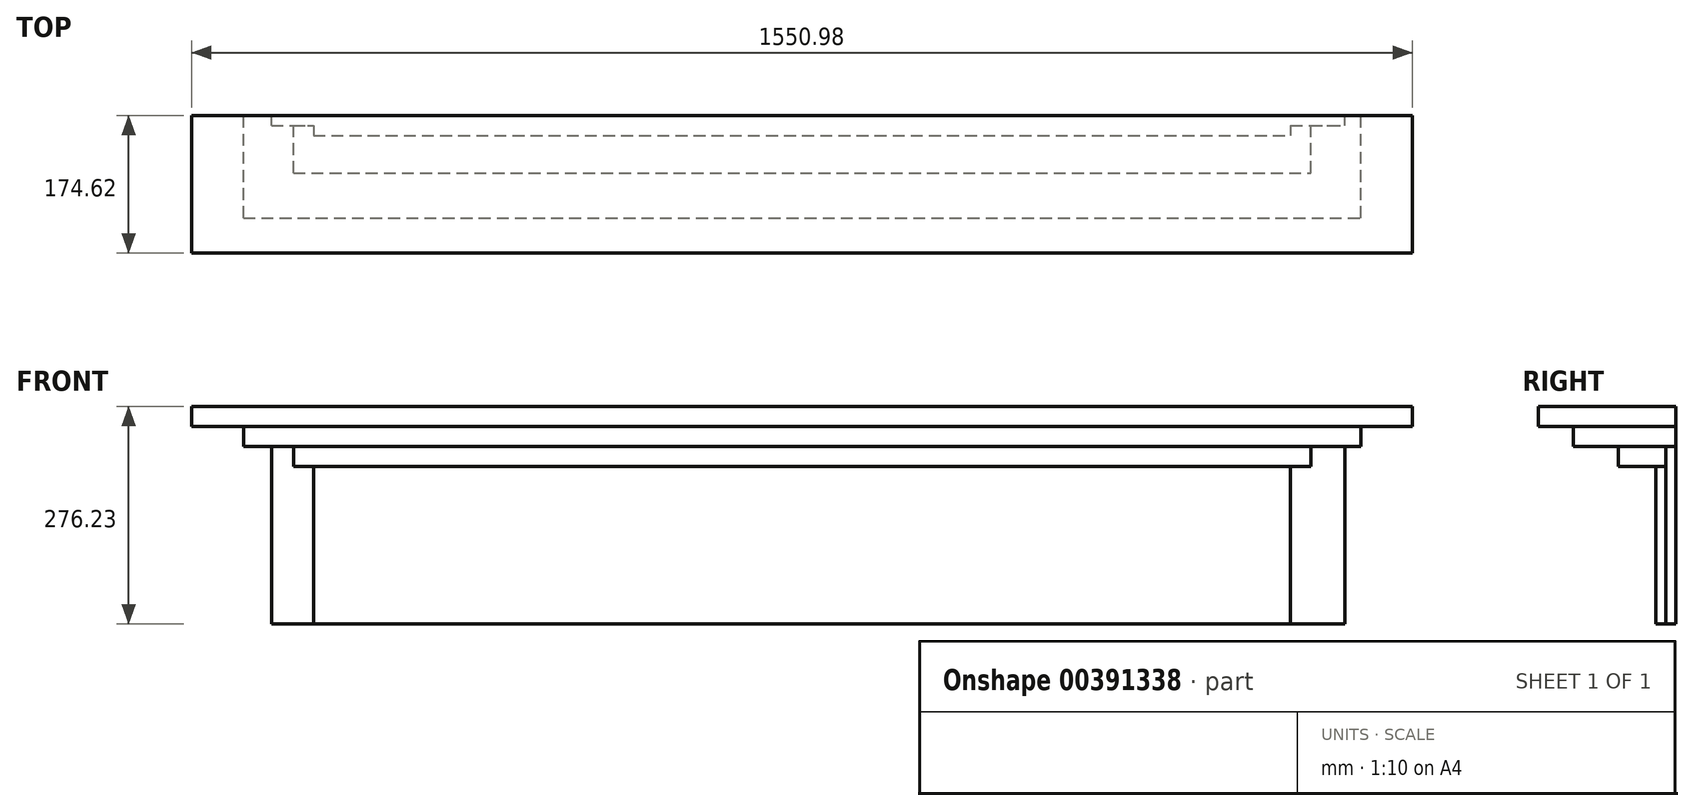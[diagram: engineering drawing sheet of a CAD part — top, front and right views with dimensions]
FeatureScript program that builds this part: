
annotation { "Feature Type Name" : "Feature", "Feature Type Description" : "" }
export const myFeature = defineFeature(function(context is Context, id is Id, definition is map)
    precondition{}
    {
        {
            var Q0;
            Q0=qCreatedBy(makeId("Front.planeOp"),FACE);
            var sketch = newSketch(context, id + "F0", { "sketchPlane" : qUnion([Q0])});
            skLineSegment(sketch, "E0.bottom", {"start": v(-775.5, 0) * mm, "end": v(775.5, 0) * mm});
            skLineSegment(sketch, "E0.top", {"start": v(-775.5, -25.4) * mm, "end": v(775.5, -25.4) * mm});
            skLineSegment(sketch, "E0.left", {"start": v(-775.5, 0) * mm, "end": v(-775.5, -25.4) * mm});
            skLineSegment(sketch, "E0.right", {"start": v(775.5, 0) * mm, "end": v(775.5, -25.4) * mm});
            skSolve(sketch);
        }
        {
            var Q0;
            Q0 = qSketchRegion(id + "F0", true);
            extrude(context, id + "F1", {"entities" : qUnion([Q0]), "depth" : 174.62 * mm});
        }
        {
            var Q0;
            Q0=qCreatedBy(makeId("Front.planeOp"),FACE);
            var sketch = newSketch(context, id + "F2", { "sketchPlane" : qUnion([Q0])});
            skLineSegment(sketch, "E1.bottom", {"start": v(-673.9, -25.4) * mm, "end": v(689.77, -25.4) * mm});
            skLineSegment(sketch, "E1.top", {"start": v(-673.9, -276.23) * mm, "end": v(689.77, -276.23) * mm});
            skLineSegment(sketch, "E1.left", {"start": v(-673.9, -25.4) * mm, "end": v(-673.9, -276.22) * mm});
            skLineSegment(sketch, "E1.right", {"start": v(689.77, -25.4) * mm, "end": v(689.77, -276.23) * mm});
            skSolve(sketch);
        }
        {
            var Q0;
            Q0=qCreatedBy(makeId("Front.planeOp"),FACE);
            var sketch = newSketch(context, id + "F3", { "sketchPlane" : qUnion([Q0])});
            skLineSegment(sketch, "E2.bottom", {"start": v(-709.61, -25.4) * mm, "end": v(709.61, -25.4) * mm});
            skLineSegment(sketch, "E2.top", {"start": v(-709.61, -50.8) * mm, "end": v(709.61, -50.8) * mm});
            skLineSegment(sketch, "E2.left", {"start": v(-709.61, -25.4) * mm, "end": v(-709.61, -50.8) * mm});
            skLineSegment(sketch, "E2.right", {"start": v(709.61, -25.4) * mm, "end": v(709.61, -50.8) * mm});
            skSolve(sketch);
        }
        {
            var Q0;
            Q0 = qSketchRegion(id + "F3", true);
            extrude(context, id + "F4", {"entities" : qUnion([Q0]), "operationType" : NewBodyOperationType.ADD, "depth" : 130.17 * mm});
        }
        {
            var Q0;
            Q0=qCreatedBy(makeId("Front.planeOp"),FACE);
            var sketch = newSketch(context, id + "F5", { "sketchPlane" : qUnion([Q0])});
            skLineSegment(sketch, "E3.bottom", {"start": v(-646.11, -50.8) * mm, "end": v(646.11, -50.8) * mm});
            skLineSegment(sketch, "E3.top", {"start": v(-646.11, -76.2) * mm, "end": v(646.11, -76.2) * mm});
            skLineSegment(sketch, "E3.left", {"start": v(-646.11, -50.8) * mm, "end": v(-646.11, -76.2) * mm});
            skLineSegment(sketch, "E3.right", {"start": v(646.11, -50.8) * mm, "end": v(646.11, -76.2) * mm});
            skSolve(sketch);
        }
        {
            var Q0;
            Q0 = qSketchRegion(id + "F5", true);
            extrude(context, id + "F6", {"entities" : qUnion([Q0]), "operationType" : NewBodyOperationType.ADD, "depth" : 73.02 * mm});
        }
        {
            var Q0;
            Q0=makeQuery(id+"F2.imprint","IMPRINT",FACE,{"disambiguationData":[TD([[makeQuery(id+"F2.imprint","IMPRINT",EDGE,{"derivedFrom":sQuery(id+"F2.wireOp",EDGE,"E1.bottom")}),-1.0]])]});
            extrude(context, id + "F7", {"entities" : qUnion([Q0]), "operationType" : NewBodyOperationType.ADD, "depth" : 25.4 * mm});
        }
        {
            var Q0;
            Q0=makeQuery(id+"F7.opExtrude","CAP_FACE",FACE,{"disambiguationData":[OSD([sQuery(id+"F2.wireOp",EDGE,"E1.bottom"),sQuery(id+"F2.wireOp",EDGE,"E1.top"),sQuery(id+"F2.wireOp",EDGE,"E1.left"),sQuery(id+"F2.wireOp",EDGE,"E1.right")])],"isStart":false});
            var sketch = newSketch(context, id + "F8", { "sketchPlane" : qUnion([Q0])});
            skLineSegment(sketch, "E4.bottom", {"start": v(-673.9, -276.22) * mm, "end": v(-620.71, -276.22) * mm});
            skLineSegment(sketch, "E4.top", {"start": v(-673.9, -50.8) * mm, "end": v(-620.71, -50.8) * mm});
            skLineSegment(sketch, "E4.left", {"start": v(-673.9, -276.22) * mm, "end": v(-673.9, -50.8) * mm});
            skLineSegment(sketch, "E4.right", {"start": v(-620.71, -276.22) * mm, "end": v(-620.71, -50.8) * mm});
            skLineSegment(sketch, "E5.bottom", {"start": v(689.77, -276.23) * mm, "end": v(620.71, -276.23) * mm});
            skLineSegment(sketch, "E5.top", {"start": v(689.77, -50.8) * mm, "end": v(620.71, -50.8) * mm});
            skLineSegment(sketch, "E5.left", {"start": v(689.77, -276.23) * mm, "end": v(689.77, -50.8) * mm});
            skLineSegment(sketch, "E5.right", {"start": v(620.71, -276.22) * mm, "end": v(620.71, -50.8) * mm});
            skSolve(sketch);
        }
        {
            var Q0;
            {var subQ1=sQuery(id+"F8.wireOp",EDGE,"E4.bottom");Q0=makeQuery(id+"F8.imprint","IMPRINT",FACE,{"disambiguationData":[TD([[makeQuery(id+"F8.imprint","IMPRINT",EDGE,{"derivedFrom":subQ1}),1.0]])]});}
            var Q1;
            {var subQ1=sQuery(id+"F8.wireOp",EDGE,"E5.bottom");Q1=makeQuery(id+"F8.imprint","IMPRINT",FACE,{"disambiguationData":[TD([[makeQuery(id+"F8.imprint","IMPRINT",EDGE,{"derivedFrom":subQ1}),1.0]])]});}
            extrude(context, id + "F9", {"entities" : qUnion([Q0, Q1]), "operationType" : NewBodyOperationType.REMOVE, "oppositeDirection" : true, "depth" : 12.7 * mm});
        }
    });
